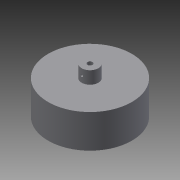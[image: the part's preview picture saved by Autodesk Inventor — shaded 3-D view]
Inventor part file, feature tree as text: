
AUTODESK INVENTOR PART (.ipt)
format: ipt  version: 2015 (Build 190159000, 159)  size: 97,280 bytes
history: native  units: in
note: dims shown in document units (in); Inventor stores cm internally (conversion verified against a paired STEP export)
features: extrude x3, sketch x2, plane x1
ambient origin geometry x8: Origin, YZ Plane, XZ Plane, XY Plane, X Axis, Y Axis, Z Axis, Center Point
bodies: Solid1 (feature_tree)
feature tree (6):
  sketch  "Sketch1"  dims[d0=3.937in d1=0.7874in]
  extrude  "Extrusion1"  Depth=0.7874in
  extrude  "Extrusion2"  Depth=0.1181in TaperAngle=0.0deg
  plane  "Work Plane1"
  extrude  "Extrusion3"  Depth=0.1181in TaperAngle=0.0deg
  sketch  "Sketch2"  dims[d2=0.2362in d3=1.5748in d4=0.0in d5=0.5906in d6=0.0in d7=90.0deg d8=0.2953in d9=0.1181in d10=1.1811in d11=0.0in]
